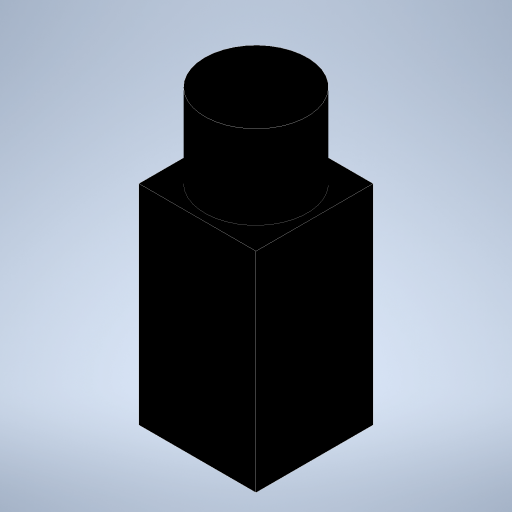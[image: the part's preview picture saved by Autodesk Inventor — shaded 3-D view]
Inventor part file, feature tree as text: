
AUTODESK INVENTOR PART (.ipt)
format: ipt  version: 2023 (Build 270158000, 158)  size: 219,136 bytes
history: native  units: in
note: dims shown in document units (in); Inventor stores cm internally (conversion verified against a paired STEP export)
features: extrude x2, sketch x1
ambient origin geometry x8: Origin, YZ Plane, XZ Plane, XY Plane, X Axis, Y Axis, Z Axis, Center Point
bodies: Solid1 (feature_tree)
feature tree (3):
  sketch  "Sketch1"  dims[d0=0.245in d1=0.14in d2=0.14in d3=0.28in d4=0.28in d5=0.7in d6=0.0in d7=0.5in d8=0.0in]
  extrude  "Extrusion1"  Depth=0.5in
  extrude  "Extrusion2"  Depth=0.5in
